# Revit family: GPB-250
name_source: partatom
category: Generic Models
revit_build: Autodesk Revit LT 2016 (Build: 20161004_0715(x64)
units: mm (PartAtom-declared; Revit-internal decimal feet)

## family parameters
Always vertical = Yes
Can host rebar = No
Cut with Voids When Loaded = No
Part Type = Normal
Room Calculation Point = No
Round Connector Dimension = Use Diameter
Shared = No
Work Plane-Based = No

## types (1)
- GPB-250
    A = 10.75 "
    B = 4.63 "
    BLADE = AA-610-215
    C = 13 "
    D = 6 "
    E = 7.5 "
    F = 8.5 "
    G = 10.25 "
    H = 4.5 "
    HOUSING = #1061  M=4.25
    J = 6 "
    K = 3.75 "
    L = 5.75 "
    MOTOR = #8413617060
    Manufacturer = REVERSOMATIC
    Model = GPB-250
    RPM = 1500
    SP/CFM = .00/259  .05/253 .10/247 .15/240  .20/234  .25/227  .30/220  .35/214  .40/206  .45/199  .50/194  .55/174
    URL = http://www.reversomatic.com

## geometry (parser evidence)
native form markers: Sweep x2
no freeform markers — native parametric forms only
